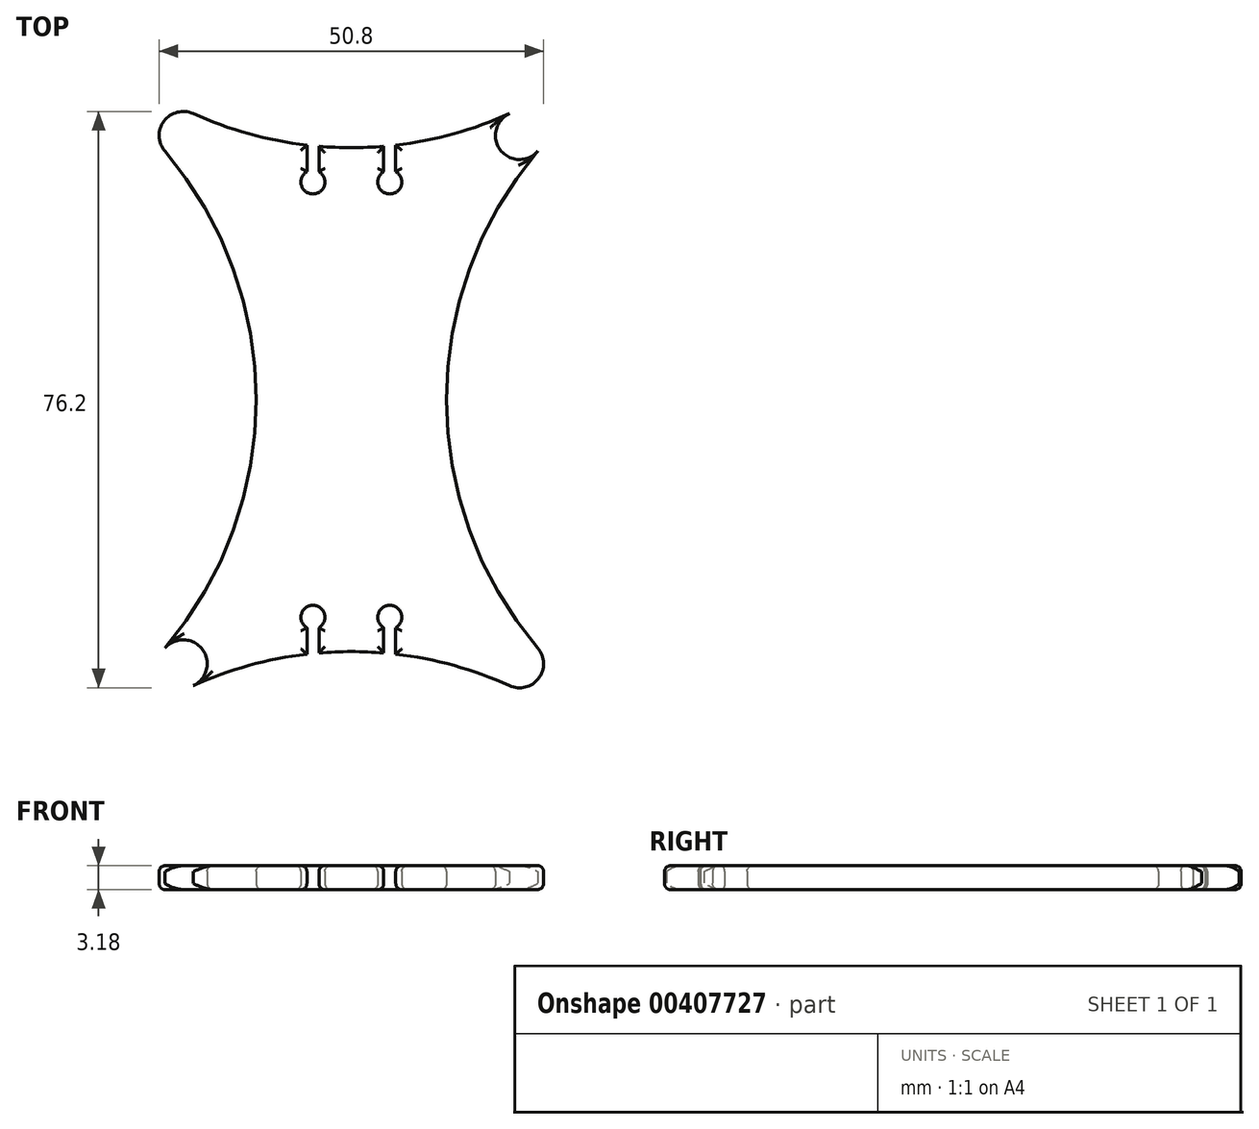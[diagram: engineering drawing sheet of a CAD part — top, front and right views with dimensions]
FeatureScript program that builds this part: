
annotation { "Feature Type Name" : "Feature", "Feature Type Description" : "" }
export const myFeature = defineFeature(function(context is Context, id is Id, definition is map)
    precondition{}
    {
        {
            var Q0;
            Q0=qCreatedBy(makeId("Top.planeOp"),FACE);
            var sketch = newSketch(context, id + "F0", { "sketchPlane" : qUnion([Q0])});
            skLineSegment(sketch, "E0.bottom", {"start": v(0, 0) * mm, "end": v(50.8, 0) * mm, "construction": true});
            skLineSegment(sketch, "E0.top", {"start": v(0, 76.2) * mm, "end": v(50.8, 76.2) * mm, "construction": true});
            skLineSegment(sketch, "E0.left", {"start": v(0, 0) * mm, "end": v(0, 76.2) * mm, "construction": true});
            skLineSegment(sketch, "E0.right", {"start": v(50.8, 0) * mm, "end": v(50.8, 76.2) * mm, "construction": true});
            skCircle(sketch, "E1", {"center": v(3.17, 73.03) * mm, "radius": 3.18 * mm});
            skLineSegment(sketch, "E2", {"start": v(25.4, 76.2) * mm, "end": v(25.4, 0) * mm, "construction": true});
            skLineSegment(sketch, "E3", {"start": v(0, 38.1) * mm, "end": v(50.8, 38.1) * mm, "construction": true});
            skCircle(sketch, "E4.MirrorC", {"center": v(47.63, 73.03) * mm, "radius": 3.18 * mm});
            skCircle(sketch, "E5.MirrorC", {"center": v(47.62, 3.17) * mm, "radius": 3.18 * mm});
            skCircle(sketch, "E6.MirrorC", {"center": v(3.17, 3.18) * mm, "radius": 3.18 * mm});
            skArc(sketch, "E7", {"start": v(4.48, 75.92) * mm, "mid": v(25.4, 71.41) * mm, "end": v(46.32, 75.92) * mm});
            skArc(sketch, "E8", {"start": v(50.05, 70.97) * mm, "mid": v(37.98, 38.1) * mm, "end": v(50.05, 5.23) * mm});
            skArc(sketch, "E9.MirrorC", {"start": v(0.75, 70.97) * mm, "mid": v(12.82, 38.1) * mm, "end": v(0.75, 5.23) * mm});
            skArc(sketch, "E10.MirrorC", {"start": v(4.48, 0.28) * mm, "mid": v(25.4, 4.79) * mm, "end": v(46.32, 0.28) * mm});
            skLineSegment(sketch, "E11", {"start": v(30.48, 70.92) * mm, "end": v(30.48, 66.88) * mm});
            skCircle(sketch, "E12", {"center": v(30.48, 66.88) * mm, "radius": 1.59 * mm});
            skLineSegment(sketch, "E13.0", {"start": v(29.69, 71.6) * mm, "end": v(29.69, 68.26) * mm});
            skLineSegment(sketch, "E14.0", {"start": v(31.27, 71.75) * mm, "end": v(31.27, 68.26) * mm});
            skLineSegment(sketch, "E15.MirrorCS", {"start": v(21.11, 71.6) * mm, "end": v(21.11, 68.26) * mm});
            skLineSegment(sketch, "E16.MirrorCS", {"start": v(19.53, 71.75) * mm, "end": v(19.53, 68.26) * mm});
            skCircle(sketch, "E17.MirrorC", {"center": v(20.32, 66.88) * mm, "radius": 1.59 * mm});
            skLineSegment(sketch, "E18.MirrorCS", {"start": v(29.69, 4.6) * mm, "end": v(29.69, 7.94) * mm});
            skLineSegment(sketch, "E19.MirrorCS", {"start": v(30.48, 5.28) * mm, "end": v(30.48, 9.32) * mm});
            skLineSegment(sketch, "E20.MirrorCS", {"start": v(31.27, 4.45) * mm, "end": v(31.27, 7.94) * mm});
            skLineSegment(sketch, "E21.MirrorCS", {"start": v(21.11, 4.6) * mm, "end": v(21.11, 7.94) * mm});
            skCircle(sketch, "E22.MirrorC", {"center": v(20.32, 9.32) * mm, "radius": 1.59 * mm});
            skCircle(sketch, "E23.MirrorC", {"center": v(30.48, 9.32) * mm, "radius": 1.59 * mm});
            skLineSegment(sketch, "E24.MirrorCS", {"start": v(19.53, 4.45) * mm, "end": v(19.53, 7.94) * mm});
            skSolve(sketch);
        }
        {
            var Q0;
            {var subQ15=sQuery(id+"F0.wireOp",EDGE,"E8");Q0=makeQuery(id+"F0.imprint","IMPRINT",FACE,{"disambiguationData":[TD([[makeQuery(id+"F0.imprint","IMPRINT",EDGE,{"derivedFrom":subQ15}),-1.0]])]});}
            var Q1;
            {var subQ0=sQuery(id+"F0.wireOp",EDGE,"E5.MirrorC");var subQ1=makeQuery(id+"F0.imprint","INTERSECT",VERTEX,{"derivedFrom":[subQ0,sQuery(id+"F0.wireOp",EDGE,"E8")]});Q1=makeQuery(id+"F0.imprint","IMPRINT",FACE,{"disambiguationData":[TD([[makeQuery(id+"F0.imprint","IMPRINT",EDGE,{"disambiguationData":[TD([[subQ1,1.0]])],"derivedFrom":subQ0}),1.0]])]});}
            var Q2;
            {var subQ0=sQuery(id+"F0.wireOp",EDGE,"E6.MirrorC");var subQ1=makeQuery(id+"F0.imprint","INTERSECT",VERTEX,{"derivedFrom":[subQ0,sQuery(id+"F0.wireOp",EDGE,"E9.MirrorC")]});Q2=makeQuery(id+"F0.imprint","IMPRINT",FACE,{"disambiguationData":[TD([[makeQuery(id+"F0.imprint","IMPRINT",EDGE,{"disambiguationData":[TD([[subQ1,1.0]])],"derivedFrom":subQ0}),-1.0]])]});}
            var Q3;
            {var subQ0=sQuery(id+"F0.wireOp",EDGE,"E4.MirrorC");var subQ1=makeQuery(id+"F0.imprint","INTERSECT",VERTEX,{"derivedFrom":[subQ0,sQuery(id+"F0.wireOp",EDGE,"E7")]});Q3=makeQuery(id+"F0.imprint","IMPRINT",FACE,{"disambiguationData":[TD([[makeQuery(id+"F0.imprint","IMPRINT",EDGE,{"disambiguationData":[TD([[subQ1,-1.0]])],"derivedFrom":subQ0}),-1.0]])]});}
            var Q4;
            {var subQ0=sQuery(id+"F0.wireOp",EDGE,"E1");var subQ1=makeQuery(id+"F0.imprint","INTERSECT",VERTEX,{"derivedFrom":[subQ0,sQuery(id+"F0.wireOp",EDGE,"E7")]});Q4=makeQuery(id+"F0.imprint","IMPRINT",FACE,{"disambiguationData":[TD([[makeQuery(id+"F0.imprint","IMPRINT",EDGE,{"disambiguationData":[TD([[subQ1,-1.0]])],"derivedFrom":subQ0}),1.0]])]});}
            extrude(context, id + "F1", {"entities" : qUnion([Q0, Q1, Q2, Q3, Q4]), "depth" : 3.17 * mm});
        }
        {
            var Q0;
            Q0=makeQuery(id+"F1.opExtrude","CAP_FACE",FACE,{"disambiguationData":[OSD([sQuery(id+"F0.wireOp",EDGE,"E1"),sQuery(id+"F0.wireOp",EDGE,"E4.MirrorC"),sQuery(id+"F0.wireOp",EDGE,"E5.MirrorC"),sQuery(id+"F0.wireOp",EDGE,"E6.MirrorC"),sQuery(id+"F0.wireOp",EDGE,"E7"),sQuery(id+"F0.wireOp",EDGE,"E8"),sQuery(id+"F0.wireOp",EDGE,"E9.MirrorC"),sQuery(id+"F0.wireOp",EDGE,"E10.MirrorC"),sQuery(id+"F0.wireOp",EDGE,"E12"),sQuery(id+"F0.wireOp",EDGE,"E13.0"),sQuery(id+"F0.wireOp",EDGE,"E14.0"),sQuery(id+"F0.wireOp",EDGE,"E15.MirrorCS"),sQuery(id+"F0.wireOp",EDGE,"E16.MirrorCS"),sQuery(id+"F0.wireOp",EDGE,"E17.MirrorC"),sQuery(id+"F0.wireOp",EDGE,"E20.MirrorCS"),sQuery(id+"F0.wireOp",EDGE,"E18.MirrorCS"),sQuery(id+"F0.wireOp",EDGE,"E24.MirrorCS"),sQuery(id+"F0.wireOp",EDGE,"E21.MirrorCS"),sQuery(id+"F0.wireOp",EDGE,"E23.MirrorC"),sQuery(id+"F0.wireOp",EDGE,"E22.MirrorC")])],"isStart":false});
            var Q1;
            Q1=makeQuery(id+"F1.opExtrude","CAP_FACE",FACE,{"disambiguationData":[OSD([sQuery(id+"F0.wireOp",EDGE,"E1"),sQuery(id+"F0.wireOp",EDGE,"E4.MirrorC"),sQuery(id+"F0.wireOp",EDGE,"E5.MirrorC"),sQuery(id+"F0.wireOp",EDGE,"E6.MirrorC"),sQuery(id+"F0.wireOp",EDGE,"E7"),sQuery(id+"F0.wireOp",EDGE,"E8"),sQuery(id+"F0.wireOp",EDGE,"E9.MirrorC"),sQuery(id+"F0.wireOp",EDGE,"E10.MirrorC"),sQuery(id+"F0.wireOp",EDGE,"E12"),sQuery(id+"F0.wireOp",EDGE,"E13.0"),sQuery(id+"F0.wireOp",EDGE,"E14.0"),sQuery(id+"F0.wireOp",EDGE,"E15.MirrorCS"),sQuery(id+"F0.wireOp",EDGE,"E16.MirrorCS"),sQuery(id+"F0.wireOp",EDGE,"E17.MirrorC"),sQuery(id+"F0.wireOp",EDGE,"E20.MirrorCS"),sQuery(id+"F0.wireOp",EDGE,"E18.MirrorCS"),sQuery(id+"F0.wireOp",EDGE,"E24.MirrorCS"),sQuery(id+"F0.wireOp",EDGE,"E21.MirrorCS"),sQuery(id+"F0.wireOp",EDGE,"E23.MirrorC"),sQuery(id+"F0.wireOp",EDGE,"E22.MirrorC")])],"isStart":true});
            fillet(context, id + "F2", {"entities" : qUnion([Q0, Q1]), "radius" : 0.8 * mm, "tangentPropagation" : true, "allowEdgeOverflow" : false});
        }
    });
